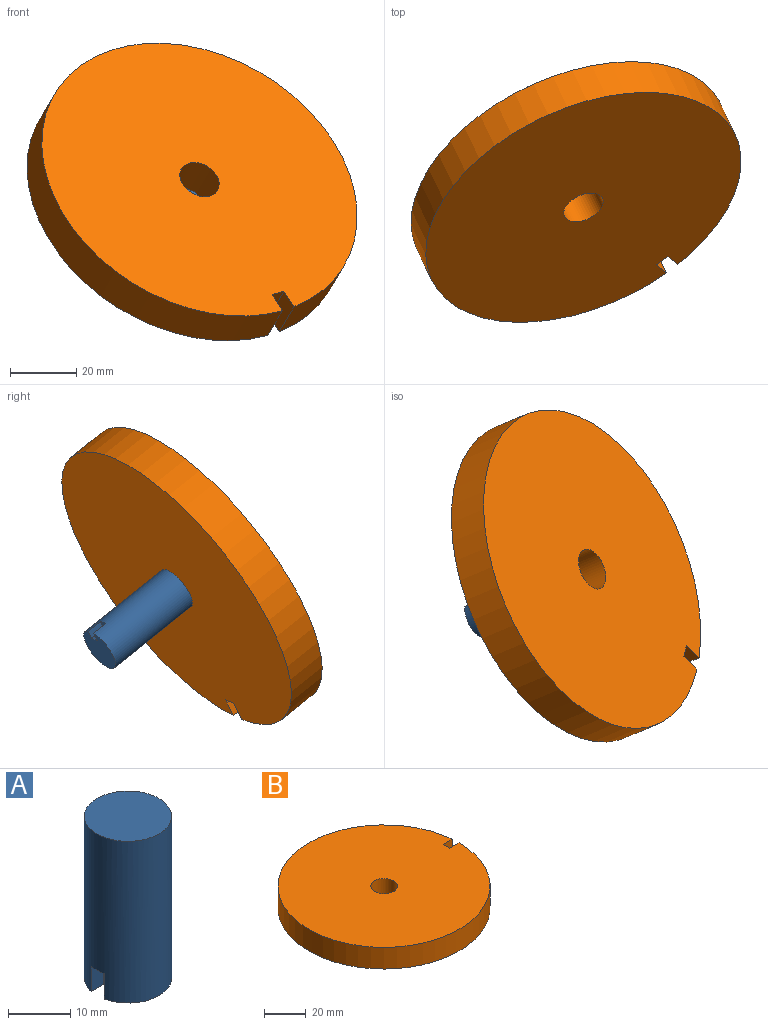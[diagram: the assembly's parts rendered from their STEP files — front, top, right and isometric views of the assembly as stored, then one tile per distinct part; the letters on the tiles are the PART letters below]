
ASSEMBLY  parts=2 mates=1
PART A: 7 faces, bbox 14x14x31.8 mm
  f0: cylinder r=7mm len=31.75mm, axis (0,0,-1), area 1381.3mm2, adj f1,f2,f3,f4,f5
  f1: plane 14x14mm, normal (0,0,1), area 153.9mm2, adj f0
  f2: plane 14x13.84mm, normal (0,0,-1), area 145.1mm2, adj f0,f4,f5,f6
  f3: plane 3x3mm, normal (0,0,-1), area 8.8mm2, adj f0,f4,f5,f6
  f4: plane 5x2.84mm, normal (0,-1,0), area 14.2mm2, adj f0,f2,f3,f6
  f5: plane 5x2.84mm, normal (0,1,0), area 14.2mm2, adj f0,f2,f3,f6
  f6: plane 5x3mm, normal (-1,0,0), area 15mm2, adj f2,f3,f4,f5
PART B: 7 faces, bbox 101.6x101.6x12.7 mm
  f0: plane 12.7x6.09mm, normal (0,-1,0), area 77.4mm2, adj f1,f4,f5,f6
  f1: cylinder r=50.8mm len=101.6mm, axis (0,0,-1), area 3997mm2, adj f0,f2,f5,f6
  f2: plane 12.7x6.29mm, normal (0,1,0), area 79.8mm2, adj f1,f4,f5,f6
  f3: cylinder r=6.35mm len=12.7mm, axis (0,0,-1), area 506.7mm2, adj f5,f6
  f4: plane 12.7x4.46mm, normal (1,0,0), area 56.6mm2, adj f0,f2,f5,f6
  f5: plane 101.6x101.6mm, normal (0,0,1), area 7952.9mm2, adj f0,f1,f2,f3,f4
  f6: plane 101.6x101.6mm, normal (0,0,-1), area 7952.9mm2, adj f0,f1,f2,f3,f4
PLACE A rot(axis=(0.5,0.6,-0.63),71.4deg) t=(-6.26,112.81,-96.86)mm
PLACE B rot(axis=(0.5,0.6,-0.63),71.4deg) t=(4.83,89.58,-78.27)mm
MATE revolute B.f1 <-> A.f0  axis (-0.35,0.73,-0.59) through (4.83,89.58,-78.27)mm
